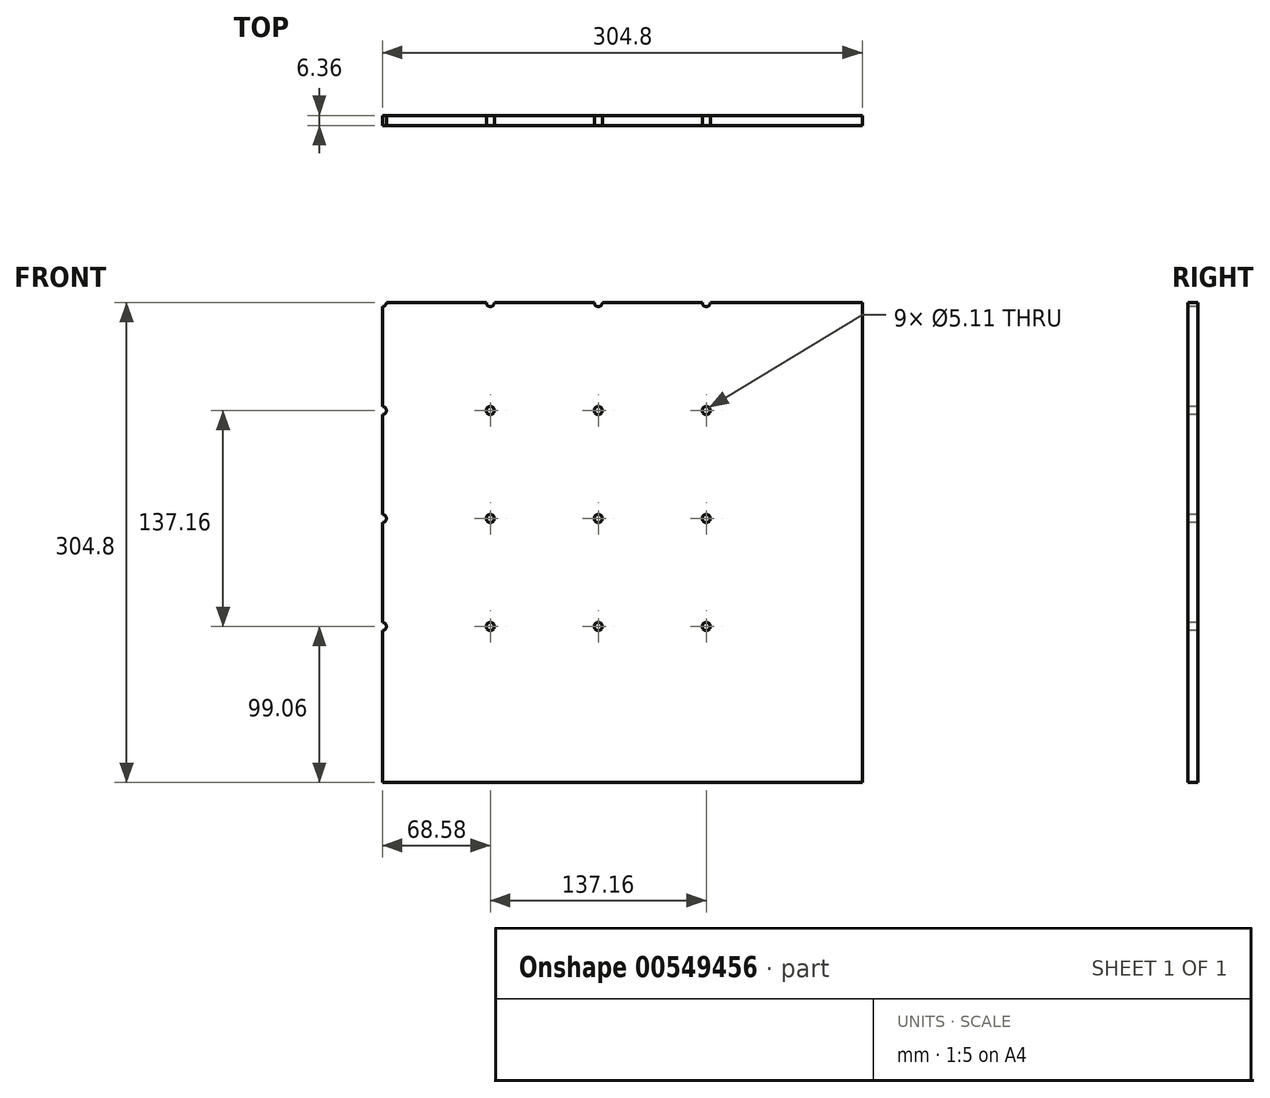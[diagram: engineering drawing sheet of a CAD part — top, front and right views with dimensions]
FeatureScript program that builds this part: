
annotation { "Feature Type Name" : "Feature", "Feature Type Description" : "" }
export const myFeature = defineFeature(function(context is Context, id is Id, definition is map)
    precondition{}
    {
        {
            var Q0;
            Q0=qCreatedBy(makeId("Front.planeOp"),FACE);
            var sketch = newSketch(context, id + "F0", { "sketchPlane" : qUnion([Q0])});
            skLineSegment(sketch, "E0.bottom", {"start": v(-152.4, 152.4) * mm, "end": v(152.4, 152.4) * mm});
            skLineSegment(sketch, "E0.top", {"start": v(-152.4, -152.4) * mm, "end": v(152.4, -152.4) * mm});
            skLineSegment(sketch, "E0.left", {"start": v(-152.4, 152.4) * mm, "end": v(-152.4, -152.4) * mm});
            skLineSegment(sketch, "E0.right", {"start": v(152.4, 152.4) * mm, "end": v(152.4, -152.4) * mm});
            skPoint(sketch, "E0.middle", {"position": v(0, 0) * mm});
            skLineSegment(sketch, "E1.bottom", {"start": v(-152.4, 152.4) * mm, "end": v(-83.82, 152.4) * mm});
            skLineSegment(sketch, "E1.left", {"start": v(-152.4, 152.4) * mm, "end": v(-152.4, 83.82) * mm});
            skPoint(sketch, "E2", {"position": v(-152.4, 152.4) * mm});
            skPoint(sketch, "E3", {"position": v(-83.82, 152.4) * mm});
            skPoint(sketch, "E4", {"position": v(-83.82, 83.82) * mm});
            skPoint(sketch, "E5", {"position": v(-152.4, 83.82) * mm});
            skPoint(sketch, "E6", {"position": v(-15.24, 83.82) * mm});
            skPoint(sketch, "E7", {"position": v(-15.24, 15.24) * mm});
            skPoint(sketch, "E8", {"position": v(-83.82, 15.24) * mm});
            skPoint(sketch, "E9", {"position": v(-152.4, 15.24) * mm});
            skPoint(sketch, "E10", {"position": v(-15.24, 152.4) * mm});
            skLineSegment(sketch, "E11.top", {"start": v(-15.24, 152.4) * mm, "end": v(53.34, 152.4) * mm});
            skPoint(sketch, "E12", {"position": v(-83.82, -53.34) * mm});
            skPoint(sketch, "E13", {"position": v(-15.24, -53.34) * mm});
            skPoint(sketch, "E14", {"position": v(53.34, 83.82) * mm});
            skPoint(sketch, "E15", {"position": v(53.34, 152.4) * mm});
            skPoint(sketch, "E16", {"position": v(53.34, 15.24) * mm});
            skPoint(sketch, "E17", {"position": v(-152.4, -53.34) * mm});
            skPoint(sketch, "E18", {"position": v(53.34, -53.34) * mm});
            skSolve(sketch);
        }
        {
            var Q0;
            Q0=makeQuery(id+"F0.imprint","IMPRINT",FACE,{"disambiguationData":[TD([[makeQuery(id+"F0.imprint","IMPRINT",EDGE,{"derivedFrom":sQuery(id+"F0.wireOp",EDGE,"E0.top")}),1.0]])]});
            extrude(context, id + "F1", {"entities" : qUnion([Q0]), "depth" : 6.35 * mm, "offsetDistance" : 25.4 * mm});
        }
        {
            var Q0;
            Q0=sQuery(id+"F0.wireOp",VERTEX,"E4");
            var Q1;
            Q1=sQuery(id+"F0.wireOp",VERTEX,"E6");
            var Q2;
            Q2=sQuery(id+"F0.wireOp",VERTEX,"E14");
            var Q3;
            Q3=sQuery(id+"F0.wireOp",VERTEX,"E8");
            var Q4;
            Q4=sQuery(id+"F0.wireOp",VERTEX,"E12");
            var Q5;
            Q5=sQuery(id+"F0.wireOp",VERTEX,"E7");
            var Q6;
            Q6=sQuery(id+"F0.wireOp",VERTEX,"E16");
            var Q7;
            Q7=sQuery(id+"F0.wireOp",VERTEX,"E18");
            var Q8;
            Q8=sQuery(id+"F0.wireOp",VERTEX,"E13");
            var Q9;
            Q9=sQuery(id+"F0.wireOp",VERTEX,"E3");
            var Q10;
            Q10=sQuery(id+"F0.wireOp",VERTEX,"E10");
            var Q11;
            Q11=sQuery(id+"F0.wireOp",VERTEX,"E15");
            var Q12;
            Q12=sQuery(id+"F0.wireOp",VERTEX,"E2");
            var Q13;
            Q13=sQuery(id+"F0.wireOp",VERTEX,"E5");
            var Q14;
            Q14=sQuery(id+"F0.wireOp",VERTEX,"E9");
            var Q15;
            Q15=sQuery(id+"F0.wireOp",VERTEX,"E17");
            var Q16;
            Q16=makeQuery(id+"F1.opExtrude","SWEPT_BODY",BODY,{"disambiguationData":[OSD([sQuery(id+"F0.wireOp",EDGE,"E0.bottom"),sQuery(id+"F0.wireOp",EDGE,"E0.top"),sQuery(id+"F0.wireOp",EDGE,"E0.left"),sQuery(id+"F0.wireOp",EDGE,"E0.right"),sQuery(id+"F0.wireOp",EDGE,"E1.bottom"),sQuery(id+"F0.wireOp",EDGE,"E1.left"),sQuery(id+"F0.wireOp",EDGE,"E11.top")])]});
            hole(context, id + "F2", {"style" : HoleStyle.SIMPLE, "endStyle" : HoleEndStyle.THROUGH, "oppositeDirection" : true, "standardTappedOrClearance" : lookupTablePath({ "standard" : "ANSI", "fit" : "Normal (ASME)", "size" : "#10", "type" : "Clearance" }), "standardBlindInLast" : lookupTablePath({ "fit" : "Free", "standard" : "ANSI", "size" : "#10", "type" : "Clearance" }), "holeDiameter" : 5.1 * mm, "majorDiameter" : 6.35 * mm, "isTappedThrough" : true, "tappedDepth" : 12.7 * mm, "tapClearance" : 3, "startFromSketch" : true, "locations" : qUnion([Q0, Q1, Q2, Q3, Q4, Q5, Q6, Q7, Q8, Q9, Q10, Q11, Q12, Q13, Q14, Q15]), "scope" : qUnion([Q16])});
        }
    });
